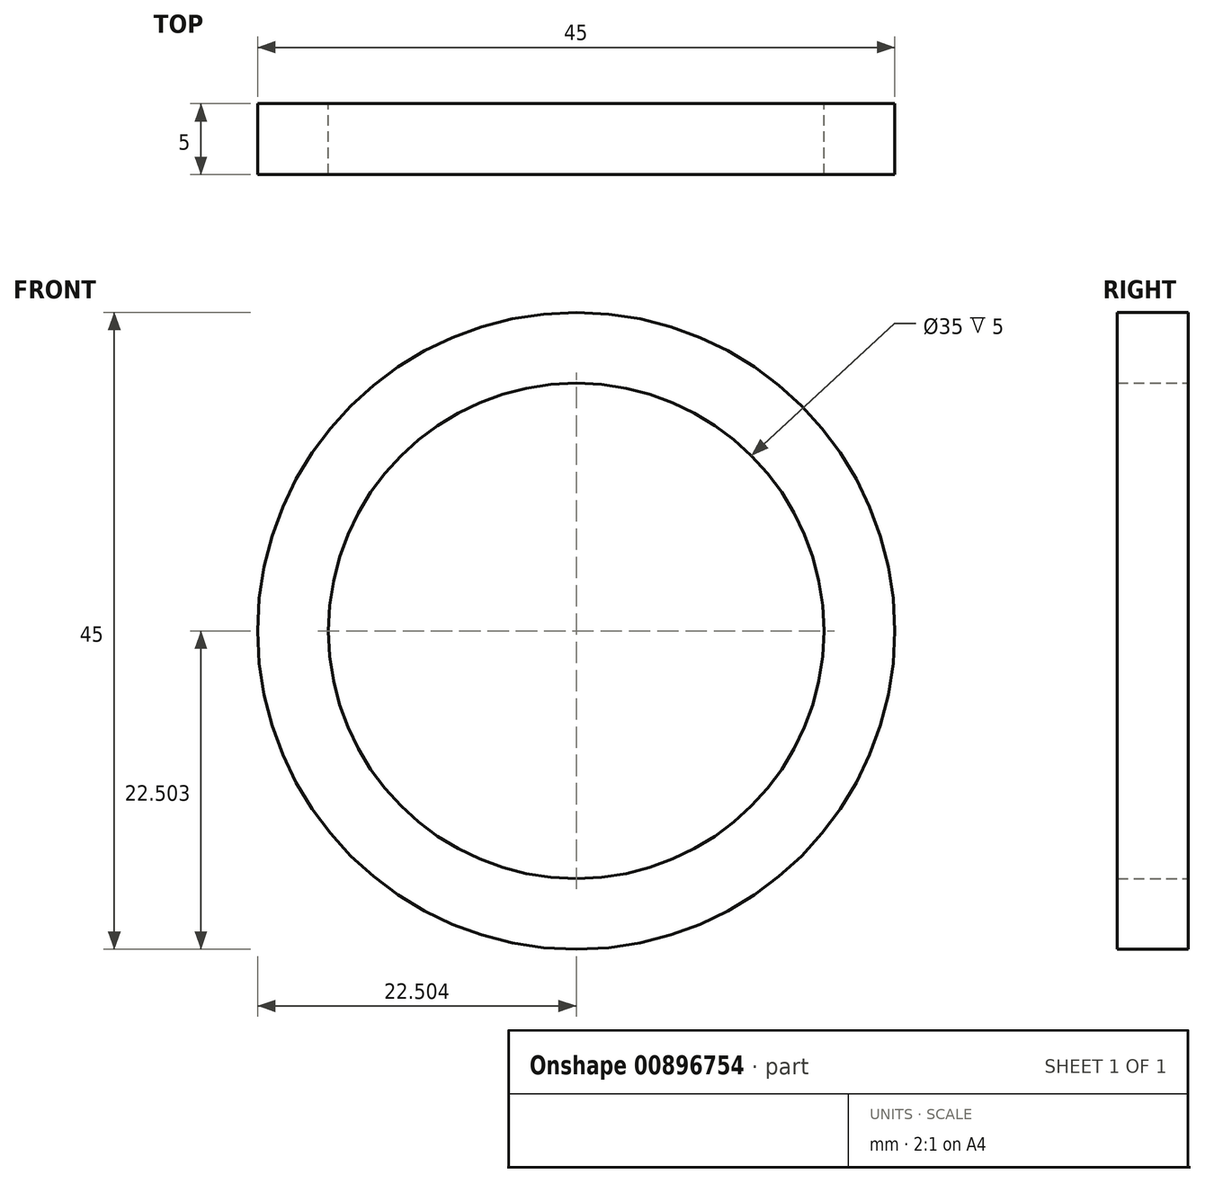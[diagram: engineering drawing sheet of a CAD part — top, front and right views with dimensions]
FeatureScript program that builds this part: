
annotation { "Feature Type Name" : "Feature", "Feature Type Description" : "" }
export const myFeature = defineFeature(function(context is Context, id is Id, definition is map)
    precondition{}
    {
        {
            var Q0;
            Q0=qCreatedBy(makeId("Front.planeOp"),FACE);
            var sketch = newSketch(context, id + "F0", { "sketchPlane" : qUnion([Q0])});
            skCircle(sketch, "E0", {"center": v(-33.15, 4.98) * mm, "radius": 22.5 * mm});
            skSolve(sketch);
        }
        {
            var Q0;
            Q0=makeQuery(id+"F0.imprint","IMPRINT",FACE,{"disambiguationData":[TD([[makeQuery(id+"F0.imprint","IMPRINT",EDGE,{"derivedFrom":sQuery(id+"F0.wireOp",EDGE,"E0")}),1.0]])]});
            extrude(context, id + "F1", {"entities" : qUnion([Q0]), "depth" : 5 * mm, "offsetDistance" : 25 * mm});
        }
        {
            var Q0;
            Q0=sQuery(id+"F0.wireOp",VERTEX,"E0.center");
            var Q1;
            Q1=makeQuery(id+"F1.opExtrude","SWEPT_BODY",BODY,{"disambiguationData":[OSD([sQuery(id+"F0.wireOp",EDGE,"E0")])]});
            hole(context, id + "F2", {"style" : HoleStyle.SIMPLE, "endStyle" : HoleEndStyle.BLIND, "oppositeDirection" : true, "holeDiameter" : 35 * mm, "majorDiameter" : 5 * mm, "holeDepth" : 5 * mm, "isTappedThrough" : true, "tappedDepth" : 12 * mm, "tapClearance" : 3, "locations" : qUnion([Q0]), "scope" : qUnion([Q1])});
        }
    });
